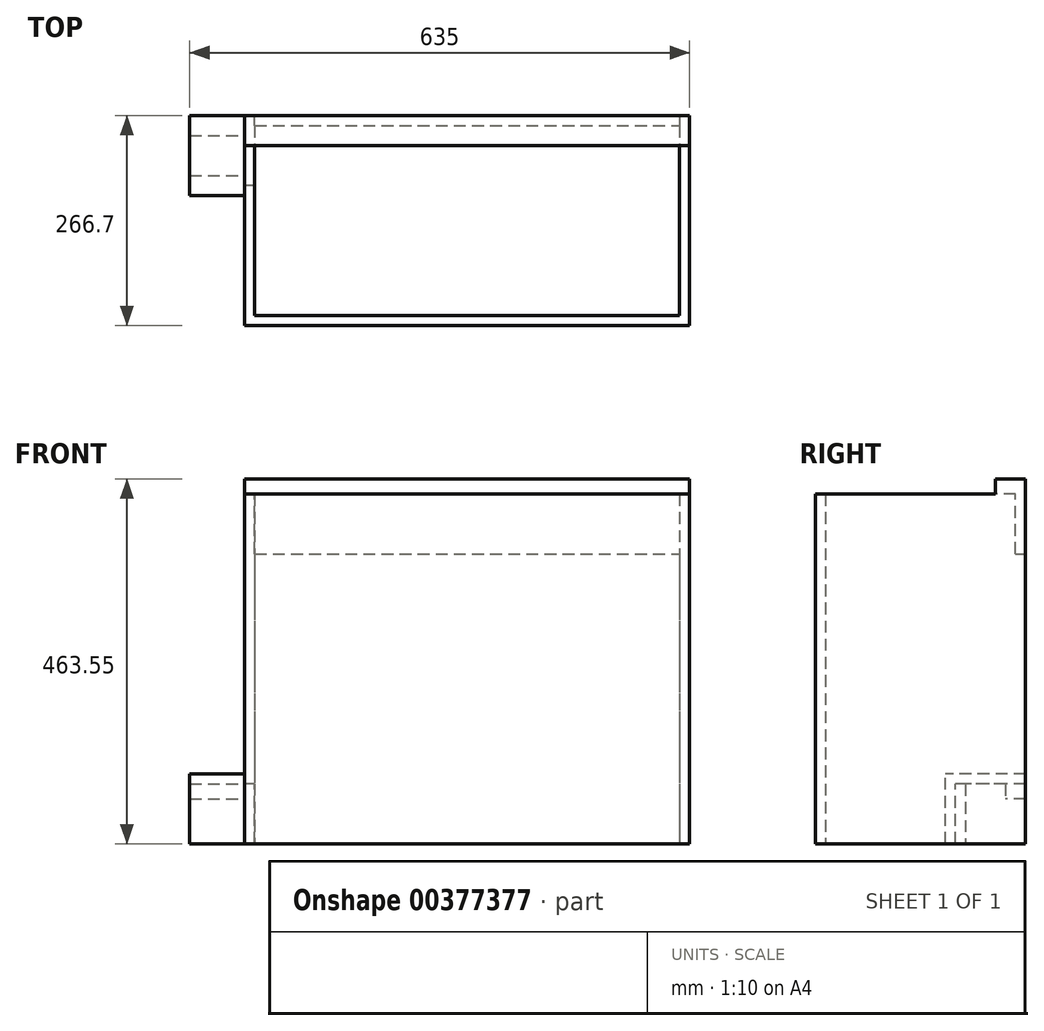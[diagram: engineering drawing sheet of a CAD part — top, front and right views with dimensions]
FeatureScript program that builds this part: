
annotation { "Feature Type Name" : "Feature", "Feature Type Description" : "" }
export const myFeature = defineFeature(function(context is Context, id is Id, definition is map)
    precondition{}
    {
        {
            var Q0;
            Q0=qCreatedBy(makeId("Top.planeOp"),FACE);
            var sketch = newSketch(context, id + "F0", { "sketchPlane" : qUnion([Q0])});
            skLineSegment(sketch, "E0.bottom", {"start": v(0, 0) * mm, "end": v(565.15, 0) * mm});
            skLineSegment(sketch, "E0.top", {"start": v(0, -279.4) * mm, "end": v(565.15, -279.4) * mm});
            skLineSegment(sketch, "E0.left", {"start": v(0, 0) * mm, "end": v(0, -279.4) * mm});
            skLineSegment(sketch, "E0.right", {"start": v(565.15, 0) * mm, "end": v(565.15, -279.4) * mm});
            skLineSegment(sketch, "E1.0", {"start": v(12.7, -12.7) * mm, "end": v(552.45, -12.7) * mm});
            skLineSegment(sketch, "E1.1", {"start": v(12.7, -12.7) * mm, "end": v(12.7, -266.7) * mm});
            skLineSegment(sketch, "E1.2", {"start": v(12.7, -266.7) * mm, "end": v(552.45, -266.7) * mm});
            skLineSegment(sketch, "E1.3", {"start": v(552.45, -12.7) * mm, "end": v(552.45, -266.7) * mm});
            skLineSegment(sketch, "E2", {"start": v(12.7, -12.7) * mm, "end": v(0, -12.7) * mm});
            skLineSegment(sketch, "E3", {"start": v(12.7, -266.7) * mm, "end": v(0, -266.7) * mm});
            skLineSegment(sketch, "E4", {"start": v(552.45, -266.7) * mm, "end": v(565.15, -266.7) * mm});
            skLineSegment(sketch, "E5", {"start": v(552.45, -12.7) * mm, "end": v(565.15, -12.7) * mm});
            skSolve(sketch);
        }
        {
            var Q0;
            Q0=makeQuery(id+"F0.imprint","IMPRINT",FACE,{"disambiguationData":[TD([[makeQuery(id+"F0.imprint","IMPRINT",EDGE,{"derivedFrom":sQuery(id+"F0.wireOp",EDGE,"E1.1")}),-1.0]])]});
            var Q1;
            {var subQ1=sQuery(id+"F0.wireOp",EDGE,"E0.top");Q1=makeQuery(id+"F0.imprint","IMPRINT",FACE,{"disambiguationData":[TD([[makeQuery(id+"F0.imprint","IMPRINT",EDGE,{"derivedFrom":subQ1}),1.0]])]});}
            var Q2;
            Q2=makeQuery(id+"F0.imprint","IMPRINT",FACE,{"disambiguationData":[TD([[makeQuery(id+"F0.imprint","IMPRINT",EDGE,{"derivedFrom":sQuery(id+"F0.wireOp",EDGE,"E1.3")}),1.0]])]});
            extrude(context, id + "F1", {"entities" : qUnion([Q0, Q1, Q2]), "depth" : 444.5 * mm});
        }
        {
            var Q0;
            Q0=makeQuery(id+"F1.opExtrude","SWEPT_FACE",FACE,{"disambiguationData":[OSD([sQuery(id+"F0.wireOp",EDGE,"E0.left")])]});
            var sketch = newSketch(context, id + "F2", { "sketchPlane" : qUnion([Q0])});
            skLineSegment(sketch, "E6.bottom", {"start": v(0, 0) * mm, "end": v(101.6, 0) * mm});
            skLineSegment(sketch, "E6.top", {"start": v(0, 76.2) * mm, "end": v(101.6, 76.2) * mm});
            skLineSegment(sketch, "E6.left", {"start": v(0, 0) * mm, "end": v(0, 76.2) * mm});
            skLineSegment(sketch, "E6.right", {"start": v(101.6, 0) * mm, "end": v(101.6, 76.2) * mm});
            skSolve(sketch);
        }
        {
            var Q0;
            Q0 = qSketchRegion(id + "F2", true);
            extrude(context, id + "F3", {"entities" : qUnion([Q0]), "operationType" : NewBodyOperationType.REMOVE, "endBound" : BoundingType.UP_TO_NEXT, "oppositeDirection" : true, "depth" : 25.4 * mm});
        }
        {
            var Q0;
            Q0=makeQuery(id+"F1.opExtrude","SWEPT_FACE",FACE,{"disambiguationData":[OSD([sQuery(id+"F0.wireOp",EDGE,"E0.left")])]});
            var sketch = newSketch(context, id + "F4", { "sketchPlane" : qUnion([Q0])});
            skLineSegment(sketch, "E7.0", {"start": v(114.3, 0) * mm, "end": v(114.3, 88.9) * mm});
            skLineSegment(sketch, "E7.1", {"start": v(12.7, 88.9) * mm, "end": v(114.3, 88.9) * mm});
            skLineSegment(sketch, "E8.bottom", {"start": v(12.7, 76.2) * mm, "end": v(38.1, 76.2) * mm});
            skLineSegment(sketch, "E8.top", {"start": v(12.7, 57.15) * mm, "end": v(38.1, 57.15) * mm});
            skLineSegment(sketch, "E8.left", {"start": v(12.7, 76.2) * mm, "end": v(12.7, 57.15) * mm});
            skLineSegment(sketch, "E8.right", {"start": v(38.1, 76.2) * mm, "end": v(38.1, 57.15) * mm});
            skLineSegment(sketch, "E9.bottom", {"start": v(101.6, 76.2) * mm, "end": v(88.9, 76.2) * mm});
            skLineSegment(sketch, "E9.top", {"start": v(101.6, 0) * mm, "end": v(88.9, 0) * mm});
            skLineSegment(sketch, "E9.left", {"start": v(101.6, 76.2) * mm, "end": v(101.6, 0) * mm});
            skLineSegment(sketch, "E9.right", {"start": v(88.9, 76.2) * mm, "end": v(88.9, 0) * mm});
            skSolve(sketch);
        }
        {
            var Q0;
            {var subQ3=sQuery(id+"F4.wireOp",EDGE,"E7.0");Q0=makeQuery(id+"F4.imprint","IMPRINT",FACE,{"disambiguationData":[TD([[makeQuery(id+"F4.imprint","IMPRINT",EDGE,{"derivedFrom":subQ3}),1.0]])]});}
            var Q1;
            Q1=makeQuery(id+"F4.imprint","IMPRINT",FACE,{"disambiguationData":[TD([[makeQuery(id+"F4.imprint","IMPRINT",EDGE,{"derivedFrom":sQuery(id+"F4.wireOp",EDGE,"E8.bottom")}),-1.0]])]});
            var Q2;
            Q2=makeQuery(id+"F4.imprint","IMPRINT",FACE,{"disambiguationData":[TD([[makeQuery(id+"F4.imprint","IMPRINT",EDGE,{"derivedFrom":sQuery(id+"F4.wireOp",EDGE,"E9.bottom")}),-1.0]])]});
            extrude(context, id + "F5", {"entities" : qUnion([Q0, Q1, Q2]), "operationType" : NewBodyOperationType.ADD, "depth" : 69.85 * mm});
        }
        {
            var Q0;
            Q0=makeQuery(id+"F1.opExtrude","SWEPT_FACE",FACE,{"disambiguationData":[OSD([sQuery(id+"F0.wireOp",EDGE,"E1.3")])]});
            var sketch = newSketch(context, id + "F6", { "sketchPlane" : qUnion([Q0])});
            skLineSegment(sketch, "E10.bottom", {"start": v(12.7, 444.5) * mm, "end": v(25.4, 444.5) * mm});
            skLineSegment(sketch, "E10.top", {"start": v(12.7, 368.3) * mm, "end": v(25.4, 368.3) * mm});
            skLineSegment(sketch, "E10.left", {"start": v(12.7, 444.5) * mm, "end": v(12.7, 368.3) * mm});
            skLineSegment(sketch, "E10.right", {"start": v(25.4, 444.5) * mm, "end": v(25.4, 368.3) * mm});
            skSolve(sketch);
        }
        {
            var Q0;
            Q0=makeQuery(id+"F6.imprint","IMPRINT",FACE,{"disambiguationData":[TD([[makeQuery(id+"F6.imprint","IMPRINT",EDGE,{"derivedFrom":sQuery(id+"F6.wireOp",EDGE,"E10.bottom")}),-1.0]])]});
            extrude(context, id + "F7", {"entities" : qUnion([Q0]), "operationType" : NewBodyOperationType.ADD, "endBound" : BoundingType.UP_TO_NEXT, "depth" : 25.4 * mm});
        }
        {
            var Q0;
            Q0=makeQuery(id+"F7.boolean.opBoolean","MERGE",FACE,{"derivedFrom":[makeQuery(id+"F1.opExtrude","CAP_FACE",FACE,{"disambiguationData":[OSD([sQuery(id+"F0.wireOp",EDGE,"E0.top"),sQuery(id+"F0.wireOp",EDGE,"E0.left"),sQuery(id+"F0.wireOp",EDGE,"E0.right"),sQuery(id+"F0.wireOp",EDGE,"E1.1"),sQuery(id+"F0.wireOp",EDGE,"E1.2"),sQuery(id+"F0.wireOp",EDGE,"E1.3"),sQuery(id+"F0.wireOp",EDGE,"E2"),sQuery(id+"F0.wireOp",EDGE,"E5")])],"isStart":false}),makeQuery(id+"F7.opExtrude","SWEPT_FACE",FACE,{"disambiguationData":[OSD([sQuery(id+"F6.wireOp",EDGE,"E10.bottom")])]})]});
            var sketch = newSketch(context, id + "F8", { "sketchPlane" : qUnion([Q0])});
            skLineSegment(sketch, "E11.bottom", {"start": v(0, -12.7) * mm, "end": v(565.15, -12.7) * mm});
            skLineSegment(sketch, "E11.top", {"start": v(0, -50.8) * mm, "end": v(565.15, -50.8) * mm});
            skLineSegment(sketch, "E11.left", {"start": v(0, -12.7) * mm, "end": v(0, -50.8) * mm});
            skLineSegment(sketch, "E11.right", {"start": v(565.15, -12.7) * mm, "end": v(565.15, -50.8) * mm});
            skSolve(sketch);
        }
        {
            var Q0;
            {var subQ3=sQuery(id+"F0.wireOp",EDGE,"E1.3");var subQ6=makeQuery(id+"F7.opExtrude","SWEPT_EDGE",EDGE,{"disambiguationData":[OSD([subQ3,sQuery(id+"F6.wireOp",EDGE,"E10.bottom"),sQuery(id+"F6.wireOp",EDGE,"E10.right")])]});Q0=makeQuery(id+"F8.imprint","IMPRINT",FACE,{"disambiguationData":[TD([[makeQuery(id+"F8.imprint","IMPRINT",EDGE,{"derivedFrom":subQ6}),-1.0]])]});}
            var Q1;
            Q1=makeQuery(id+"F8.imprint","IMPRINT",FACE,{"disambiguationData":[TD([[makeQuery(id+"F8.imprint","IMPRINT",EDGE,{"derivedFrom":sQuery(id+"F8.wireOp",EDGE,"E11.bottom")}),1.0]])]});
            extrude(context, id + "F9", {"entities" : qUnion([Q0, Q1]), "operationType" : NewBodyOperationType.ADD, "depth" : 19.05 * mm});
        }
    });
